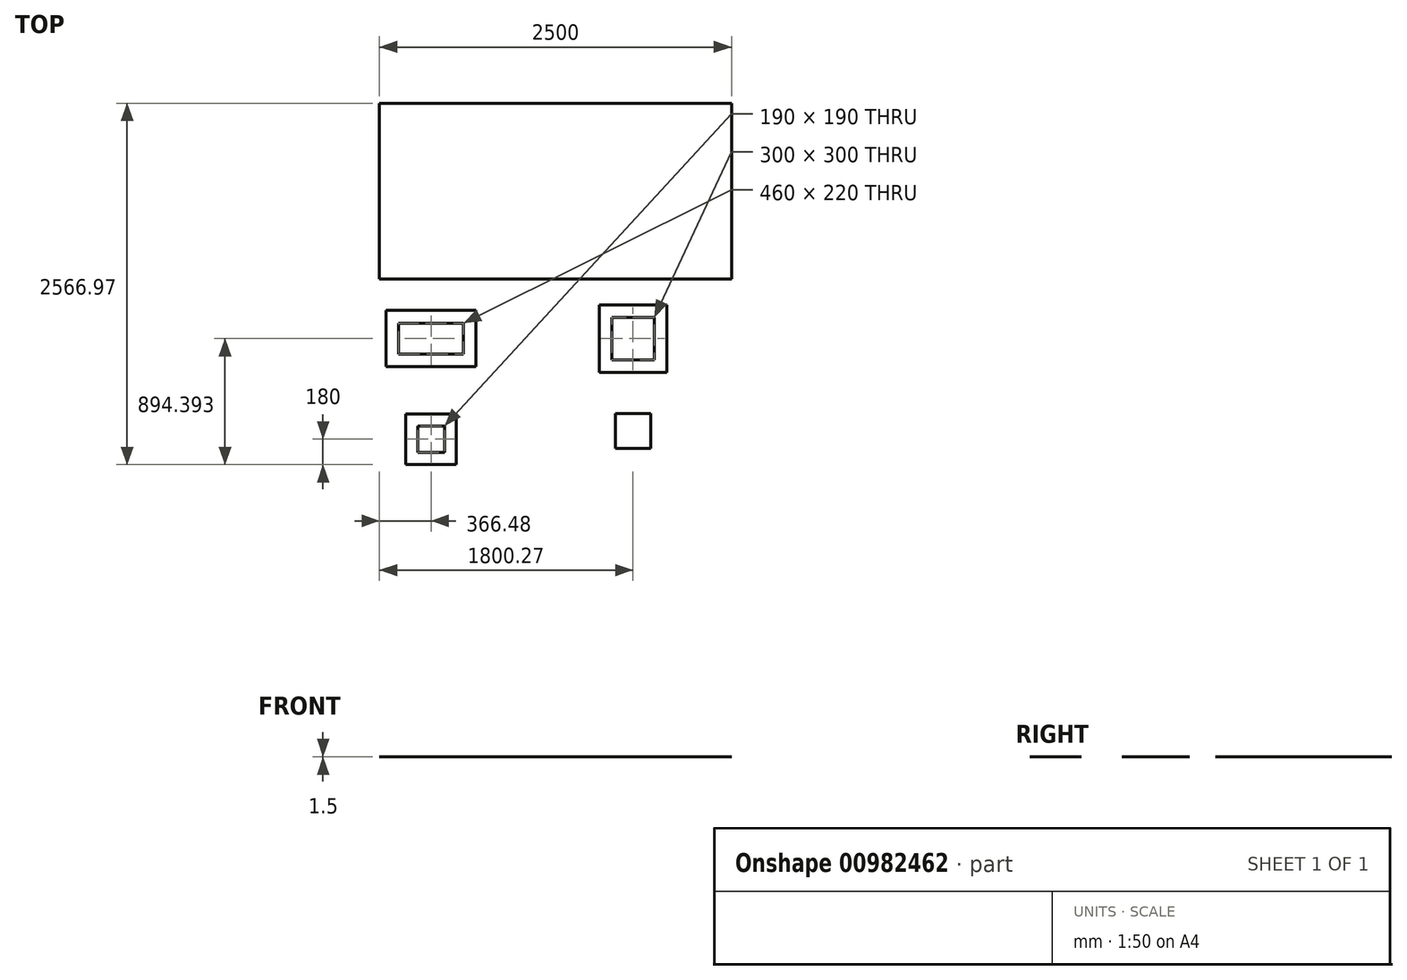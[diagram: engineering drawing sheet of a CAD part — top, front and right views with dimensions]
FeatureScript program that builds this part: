
annotation { "Feature Type Name" : "Feature", "Feature Type Description" : "" }
export const myFeature = defineFeature(function(context is Context, id is Id, definition is map)
    precondition{}
    {
        {
            var Q0;
            Q0=qCreatedBy(makeId("Top.planeOp"),FACE);
            var sketch = newSketch(context, id + "F0", { "sketchPlane" : qUnion([Q0])});
            skLineSegment(sketch, "E0.bottom", {"start": v(1526.6, 325.7) * mm, "end": v(1046.6, 325.7) * mm});
            skLineSegment(sketch, "E0.top", {"start": v(1526.6, 805.7) * mm, "end": v(1046.6, 805.7) * mm});
            skLineSegment(sketch, "E0.left", {"start": v(1526.6, 325.7) * mm, "end": v(1526.6, 805.7) * mm});
            skLineSegment(sketch, "E0.right", {"start": v(1046.6, 325.7) * mm, "end": v(1046.6, 805.7) * mm});
            skPoint(sketch, "E0.middle", {"position": v(1286.6, 565.7) * mm});
            skLineSegment(sketch, "E1.bottom", {"start": v(1136.6, 415.7) * mm, "end": v(1436.6, 415.7) * mm});
            skLineSegment(sketch, "E1.top", {"start": v(1136.6, 715.7) * mm, "end": v(1436.6, 715.7) * mm});
            skLineSegment(sketch, "E1.left", {"start": v(1136.6, 415.7) * mm, "end": v(1136.6, 715.7) * mm});
            skLineSegment(sketch, "E1.right", {"start": v(1436.6, 415.7) * mm, "end": v(1436.6, 715.7) * mm});
            skLineSegment(sketch, "E2.bottom", {"start": v(-467.2, 365.7) * mm, "end": v(172.8, 365.7) * mm});
            skLineSegment(sketch, "E2.top", {"start": v(-467.2, 765.7) * mm, "end": v(172.8, 765.7) * mm});
            skLineSegment(sketch, "E2.left", {"start": v(-467.2, 365.7) * mm, "end": v(-467.2, 765.7) * mm});
            skLineSegment(sketch, "E2.right", {"start": v(172.8, 365.7) * mm, "end": v(172.8, 765.7) * mm});
            skPoint(sketch, "E2.middle", {"position": v(-147.2, 565.7) * mm});
            skLineSegment(sketch, "E3.bottom", {"start": v(-377.2, 455.7) * mm, "end": v(82.8, 455.7) * mm});
            skLineSegment(sketch, "E3.top", {"start": v(-377.2, 675.7) * mm, "end": v(82.8, 675.7) * mm});
            skLineSegment(sketch, "E3.left", {"start": v(-377.2, 455.7) * mm, "end": v(-377.2, 675.7) * mm});
            skLineSegment(sketch, "E3.right", {"start": v(82.8, 455.7) * mm, "end": v(82.8, 675.7) * mm});
            skLineSegment(sketch, "E4.bottom", {"start": v(-327.2, -328.7) * mm, "end": v(32.8, -328.7) * mm});
            skLineSegment(sketch, "E4.top", {"start": v(-327.2, 31.3) * mm, "end": v(32.8, 31.3) * mm});
            skLineSegment(sketch, "E4.left", {"start": v(-327.2, -328.7) * mm, "end": v(-327.2, 31.3) * mm});
            skLineSegment(sketch, "E4.right", {"start": v(32.8, -328.7) * mm, "end": v(32.8, 31.3) * mm});
            skPoint(sketch, "E4.middle", {"position": v(-147.2, -148.7) * mm});
            skLineSegment(sketch, "E5.bottom", {"start": v(-242.2, -243.7) * mm, "end": v(-52.2, -243.7) * mm});
            skLineSegment(sketch, "E5.top", {"start": v(-242.2, -53.7) * mm, "end": v(-52.2, -53.7) * mm});
            skLineSegment(sketch, "E5.left", {"start": v(-242.2, -243.7) * mm, "end": v(-242.2, -53.7) * mm});
            skLineSegment(sketch, "E5.right", {"start": v(-52.2, -243.7) * mm, "end": v(-52.2, -53.7) * mm});
            skLineSegment(sketch, "E6.bottom", {"start": v(1161.6, -215.38) * mm, "end": v(1411.6, -215.38) * mm});
            skLineSegment(sketch, "E6.top", {"start": v(1161.6, 34.62) * mm, "end": v(1411.6, 34.62) * mm});
            skLineSegment(sketch, "E6.left", {"start": v(1161.6, -215.38) * mm, "end": v(1161.6, 34.62) * mm});
            skLineSegment(sketch, "E6.right", {"start": v(1411.6, -215.38) * mm, "end": v(1411.6, 34.62) * mm});
            skPoint(sketch, "E6.middle", {"position": v(1286.6, -90.38) * mm});
            skSolve(sketch);
        }
        {
            var Q0;
            Q0=makeQuery(id+"F0.imprint","IMPRINT",FACE,{"disambiguationData":[TD([[makeQuery(id+"F0.imprint","IMPRINT",EDGE,{"derivedFrom":sQuery(id+"F0.wireOp",EDGE,"E2.bottom")}),1.0]])]});
            extrude(context, id + "F1", {"entities" : qUnion([Q0]), "depth" : 1.5 * mm, "offsetDistance" : 25 * mm});
        }
        {
            var Q0;
            Q0=makeQuery(id+"F0.imprint","IMPRINT",FACE,{"disambiguationData":[TD([[makeQuery(id+"F0.imprint","IMPRINT",EDGE,{"derivedFrom":sQuery(id+"F0.wireOp",EDGE,"E0.bottom")}),-1.0]])]});
            var Q1;
            Q1=makeQuery(id+"F0.imprint","IMPRINT",FACE,{"disambiguationData":[TD([[makeQuery(id+"F0.imprint","IMPRINT",EDGE,{"derivedFrom":sQuery(id+"F0.wireOp",EDGE,"E6.bottom")}),1.0]])]});
            var Q2;
            Q2=makeQuery(id+"F0.imprint","IMPRINT",FACE,{"disambiguationData":[TD([[makeQuery(id+"F0.imprint","IMPRINT",EDGE,{"derivedFrom":sQuery(id+"F0.wireOp",EDGE,"E4.bottom")}),1.0]])]});
            extrude(context, id + "F2", {"entities" : qUnion([Q0, Q1, Q2]), "depth" : 1.5 * mm, "offsetDistance" : 25 * mm});
        }
        {
            var Q0;
            Q0=qCreatedBy(makeId("Top.planeOp"),FACE);
            var sketch = newSketch(context, id + "F3", { "sketchPlane" : qUnion([Q0])});
            skLineSegment(sketch, "E7.bottom", {"start": v(-513.67, 2238.27) * mm, "end": v(1986.33, 2238.27) * mm});
            skLineSegment(sketch, "E7.top", {"start": v(-513.67, 988.27) * mm, "end": v(1986.33, 988.27) * mm});
            skLineSegment(sketch, "E7.left", {"start": v(-513.67, 2238.27) * mm, "end": v(-513.67, 988.27) * mm});
            skLineSegment(sketch, "E7.right", {"start": v(1986.33, 2238.27) * mm, "end": v(1986.33, 988.27) * mm});
            skSolve(sketch);
        }
        {
            var Q0;
            Q0=makeQuery(id+"F3.imprint","IMPRINT",FACE,{"disambiguationData":[TD([[makeQuery(id+"F3.imprint","IMPRINT",EDGE,{"derivedFrom":sQuery(id+"F3.wireOp",EDGE,"E7.bottom")}),-1.0]])]});
            extrude(context, id + "F4", {"entities" : qUnion([Q0]), "depth" : 1.5 * mm, "offsetDistance" : 25 * mm});
        }
    });
